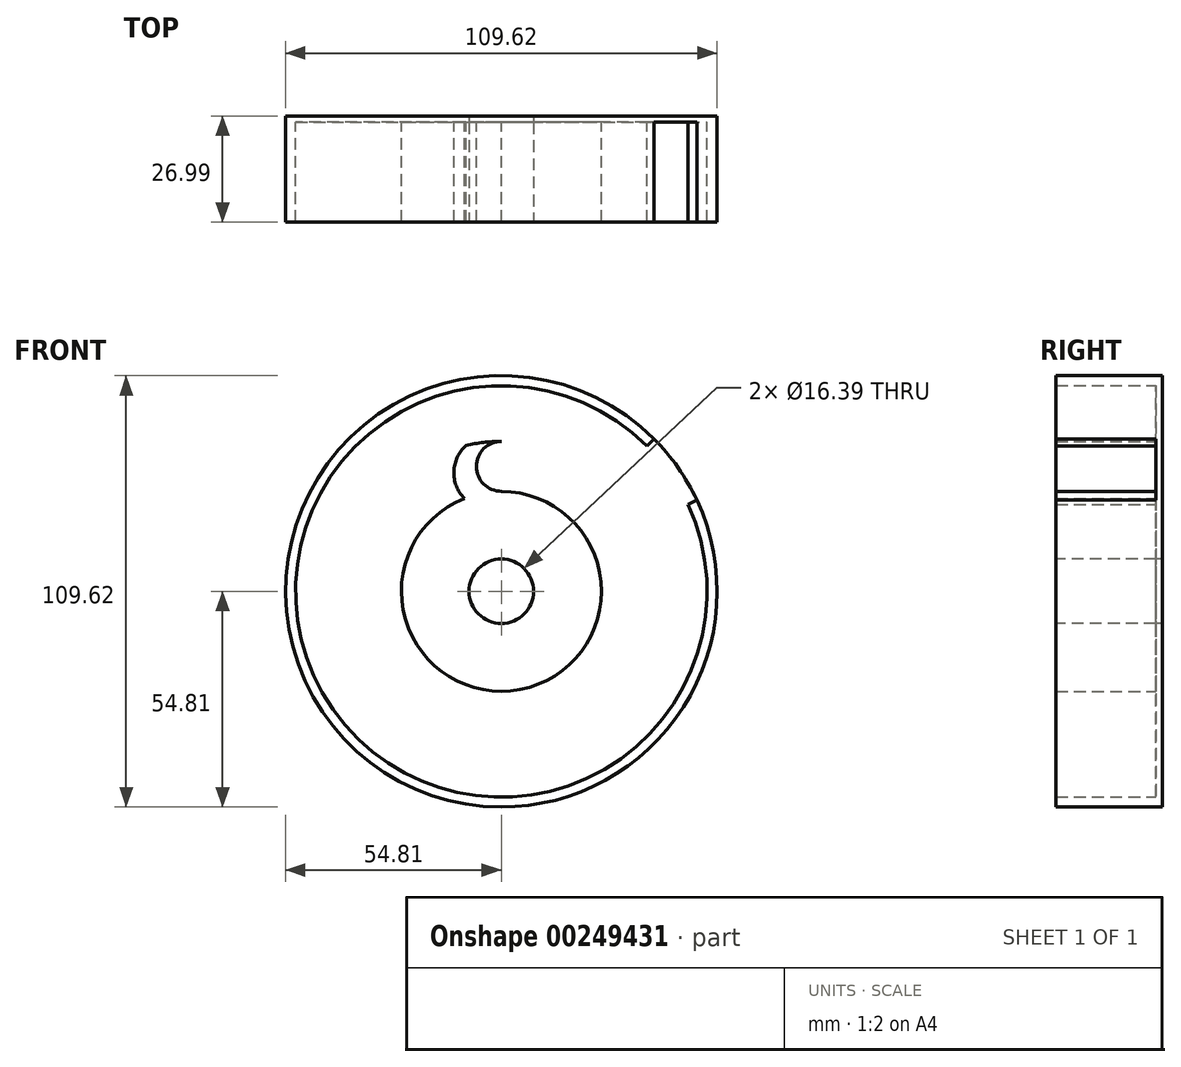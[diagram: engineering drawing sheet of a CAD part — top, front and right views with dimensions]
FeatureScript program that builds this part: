
annotation { "Feature Type Name" : "Feature", "Feature Type Description" : "" }
export const myFeature = defineFeature(function(context is Context, id is Id, definition is map)
    precondition{}
    {
        {
            var Q0;
            Q0=qCreatedBy(makeId("Front.planeOp"),FACE);
            var sketch = newSketch(context, id + "F0", { "sketchPlane" : qUnion([Q0])});
            skCircle(sketch, "E0", {"center": v(0, 0) * mm, "radius": 25.4 * mm});
            skSolve(sketch);
        }
        {
            var Q0;
            Q0 = qSketchRegion(id + "F0", true);
            extrude(context, id + "F1", {"entities" : qUnion([Q0]), "depth" : 25.4 * mm});
        }
        {
            var Q0;
            Q0=qCreatedBy(makeId("Front.planeOp"),FACE);
            var sketch = newSketch(context, id + "F2", { "sketchPlane" : qUnion([Q0])});
            skCircle(sketch, "E1", {"center": v(0, 0) * mm, "radius": 38.1 * mm, "construction": true});
            skArc(sketch, "E2", {"start": v(0, 38.1) * mm, "mid": v(-6.35, 31.75) * mm, "end": v(0, 25.4) * mm});
            skArc(sketch, "E3", {"start": v(-8.98, 37.03) * mm, "mid": v(-12.08, 30.4) * mm, "end": v(-9.42, 23.59) * mm});
            skArc(sketch, "E4", {"start": v(0, 25.4) * mm, "mid": v(-4.8, 24.94) * mm, "end": v(-9.42, 23.59) * mm});
            skArc(sketch, "E5", {"start": v(0, 38.1) * mm, "mid": v(-4.52, 37.83) * mm, "end": v(-8.98, 37.03) * mm});
            skSolve(sketch);
        }
        {
            var Q0;
            Q0=makeQuery(id+"F2.imprint","IMPRINT",FACE,{"disambiguationData":[TD([[makeQuery(id+"F2.imprint","IMPRINT",EDGE,{"derivedFrom":sQuery(id+"F2.wireOp",EDGE,"E2")}),-1.0]])]});
            var Q1;
            Q1=makeQuery(id+"F1.opExtrude","CAP_FACE",FACE,{"disambiguationData":[OSD([sQuery(id+"F0.wireOp",EDGE,"E0")])],"isStart":false});
            extrude(context, id + "F3", {"entities" : qUnion([Q0]), "operationType" : NewBodyOperationType.ADD, "endBound" : BoundingType.UP_TO_SURFACE, "endBoundEntityFace" : qUnion([Q1]), "depth" : 25.4 * mm});
        }
        {
            var Q0;
            Q0=qCreatedBy(makeId("Right.planeOp"),FACE);
            var sketch = newSketch(context, id + "F4", { "sketchPlane" : qUnion([Q0])});
            skLineSegment(sketch, "E6", {"start": v(0, 0) * mm, "end": v(-25.12, 0) * mm, "construction": true});
            skSolve(sketch);
        }
        {
            var Q0;
            Q0=qCreatedBy(makeId("Front.planeOp"),FACE);
            var sketch = newSketch(context, id + "F5", { "sketchPlane" : qUnion([Q0])});
            skCircle(sketch, "E7", {"center": v(0, 0) * mm, "radius": 54.8 * mm});
            skSolve(sketch);
        }
        {
            var Q0;
            Q0=makeQuery(id+"F5.imprint","IMPRINT",FACE,{"disambiguationData":[TD([[makeQuery(id+"F5.imprint","IMPRINT",EDGE,{"derivedFrom":sQuery(id+"F5.wireOp",EDGE,"E7")}),1.0]])]});
            extrude(context, id + "F6", {"entities" : qUnion([Q0]), "oppositeDirection" : true, "depth" : 1.59 * mm});
        }
        {
            var Q0;
            Q0=makeQuery(id+"F6.opExtrude","CAP_FACE",FACE,{"disambiguationData":[OSD([sQuery(id+"F5.wireOp",EDGE,"E7")])],"isStart":true});
            var sketch = newSketch(context, id + "F7", { "sketchPlane" : qUnion([Q0])});
            skCircle(sketch, "E8", {"center": v(0, 0) * mm, "radius": 54.8 * mm});
            skCircle(sketch, "E9", {"center": v(0, 0) * mm, "radius": 52.27 * mm});
            skSolve(sketch);
        }
        {
            var Q0;
            Q0 = qSketchRegion(id + "F7", true);
            extrude(context, id + "F8", {"entities" : qUnion([Q0]), "operationType" : NewBodyOperationType.ADD, "depth" : 25.4 * mm});
        }
        {
            var Q0;
            {var subQ0=sQuery(id+"F0.wireOp",EDGE,"E0");Q0=makeQuery(id+"FHIkrwmkjbmAIoa_1.7.F3.boolean.opBoolean","MERGE",FACE,{"derivedFrom":[makeQuery(id+"FHIkrwmkjbmAIoa_1.6.F3.boolean.opBoolean","MERGE",FACE,{"derivedFrom":[makeQuery(id+"FHIkrwmkjbmAIoa_1.5.F3.boolean.opBoolean","MERGE",FACE,{"derivedFrom":[makeQuery(id+"FHIkrwmkjbmAIoa_1.4.F3.boolean.opBoolean","MERGE",FACE,{"derivedFrom":[makeQuery(id+"FHIkrwmkjbmAIoa_1.3.F3.boolean.opBoolean","MERGE",FACE,{"derivedFrom":[makeQuery(id+"FHIkrwmkjbmAIoa_1.2.F3.boolean.opBoolean","MERGE",FACE,{"derivedFrom":[makeQuery(id+"FHIkrwmkjbmAIoa_1.1.F3.boolean.opBoolean","MERGE",FACE,{"derivedFrom":[makeQuery(id+"F3.boolean.opBoolean","MERGE",FACE,{"derivedFrom":[makeQuery(id+"F1.opExtrude","CAP_FACE",FACE,{"disambiguationData":[OSD([subQ0])],"isStart":false}),makeQuery(id+"F3.opExtrude","CAP_FACE",FACE,{"disambiguationData":[OSD([subQ0])],"isStart":false})]}),makeQuery(id+"FHIkrwmkjbmAIoa_1.1.F3.opExtrude","CAP_FACE",FACE,{"disambiguationData":[OSD([subQ0])],"isStart":false})]}),makeQuery(id+"FHIkrwmkjbmAIoa_1.2.F3.opExtrude","CAP_FACE",FACE,{"disambiguationData":[OSD([subQ0])],"isStart":false})]}),makeQuery(id+"FHIkrwmkjbmAIoa_1.3.F3.opExtrude","CAP_FACE",FACE,{"disambiguationData":[OSD([subQ0])],"isStart":false})]}),makeQuery(id+"FHIkrwmkjbmAIoa_1.4.F3.opExtrude","CAP_FACE",FACE,{"disambiguationData":[OSD([subQ0])],"isStart":false})]}),makeQuery(id+"FHIkrwmkjbmAIoa_1.5.F3.opExtrude","CAP_FACE",FACE,{"disambiguationData":[OSD([subQ0])],"isStart":false})]}),makeQuery(id+"FHIkrwmkjbmAIoa_1.6.F3.opExtrude","CAP_FACE",FACE,{"disambiguationData":[OSD([subQ0])],"isStart":false})]}),makeQuery(id+"FHIkrwmkjbmAIoa_1.7.F3.opExtrude","CAP_FACE",FACE,{"disambiguationData":[OSD([subQ0])],"isStart":false})]});}
            var sketch = newSketch(context, id + "F9", { "sketchPlane" : qUnion([Q0])});
            skCircle(sketch, "E10", {"center": v(0, 0) * mm, "radius": 8.2 * mm});
            skSolve(sketch);
        }
        {
            var Q0;
            Q0=makeQuery(id+"F9.imprint","IMPRINT",FACE,{"disambiguationData":[TD([[makeQuery(id+"F9.imprint","IMPRINT",EDGE,{"derivedFrom":sQuery(id+"F9.wireOp",EDGE,"E10")}),1.0]])]});
            extrude(context, id + "F10", {"entities" : qUnion([Q0]), "operationType" : NewBodyOperationType.REMOVE, "endBound" : BoundingType.THROUGH_ALL, "oppositeDirection" : true, "depth" : 25.4 * mm});
        }
        {
            var Q0;
            Q0=makeQuery(id+"F6.opExtrude","CAP_FACE",FACE,{"disambiguationData":[OSD([sQuery(id+"F5.wireOp",EDGE,"E7")])],"isStart":true});
            var sketch = newSketch(context, id + "F11", { "sketchPlane" : qUnion([Q0])});
            skLineSegment(sketch, "E11", {"start": v(0, 0) * mm, "end": v(38.75, 38.75) * mm, "construction": true});
            skLineSegment(sketch, "E12", {"start": v(0, 0) * mm, "end": v(49.65, 23.2) * mm, "construction": true});
            skArc(sketch, "E13", {"start": v(49.65, 23.2) * mm, "mid": v(44.88, 31.45) * mm, "end": v(38.75, 38.75) * mm});
            skArc(sketch, "E14", {"start": v(47.35, 22.12) * mm, "mid": v(42.8, 30) * mm, "end": v(36.96, 36.96) * mm});
            skLineSegment(sketch, "E15", {"start": v(38.75, 38.75) * mm, "end": v(36.96, 36.96) * mm});
            skLineSegment(sketch, "E16", {"start": v(49.65, 23.2) * mm, "end": v(47.35, 22.12) * mm});
            skSolve(sketch);
        }
        {
            var Q0;
            Q0 = qSketchRegion(id + "F11", true);
            var Q1;
            Q1=makeQuery(id+"F8.opExtrude","CAP_FACE",FACE,{"disambiguationData":[OSD([sQuery(id+"F7.wireOp",EDGE,"E8"),sQuery(id+"F7.wireOp",EDGE,"E9")])],"isStart":false});
            extrude(context, id + "F12", {"entities" : qUnion([Q0]), "operationType" : NewBodyOperationType.REMOVE, "endBound" : BoundingType.UP_TO_SURFACE, "endBoundEntityFace" : qUnion([Q1]), "depth" : 25.4 * mm});
        }
    });
